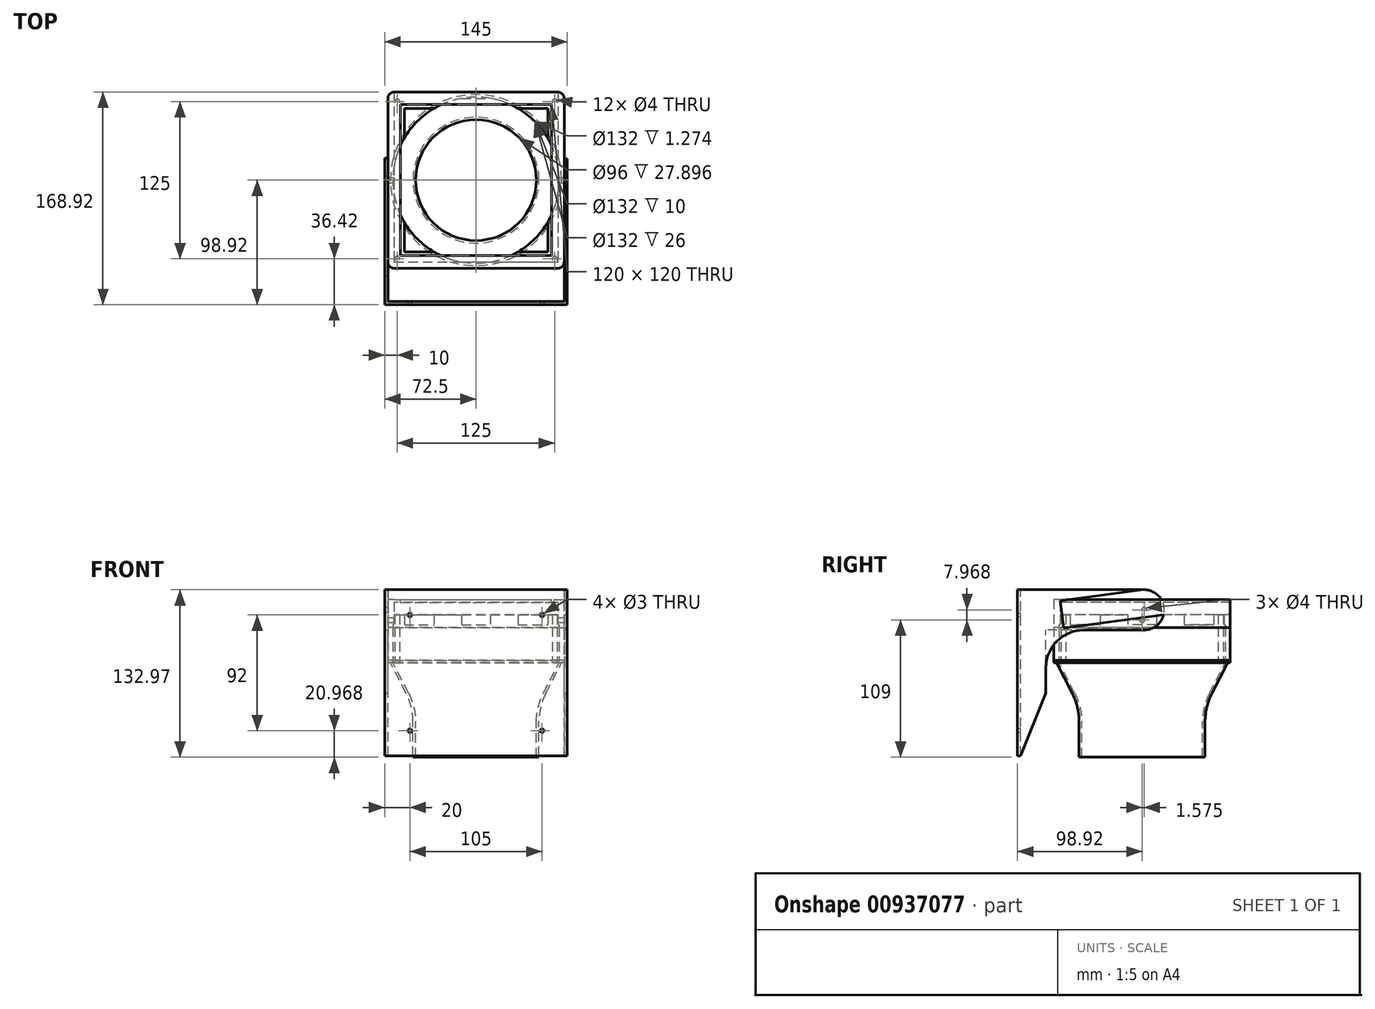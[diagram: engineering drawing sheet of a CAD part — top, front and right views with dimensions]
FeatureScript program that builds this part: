
annotation { "Feature Type Name" : "Feature", "Feature Type Description" : "" }
export const myFeature = defineFeature(function(context is Context, id is Id, definition is map)
    precondition{}
    {
        {
            var Q0;
            Q0=qCreatedBy(makeId("Top.planeOp"),FACE);
            var sketch = newSketch(context, id + "F0", { "sketchPlane" : qUnion([Q0])});
            skCircle(sketch, "E0", {"center": v(0, 0) * mm, "radius": 66 * mm});
            skLineSegment(sketch, "E1.bottom", {"start": v(-70, 70) * mm, "end": v(70, 70) * mm});
            skLineSegment(sketch, "E1.top", {"start": v(-70, -70) * mm, "end": v(70, -70) * mm});
            skLineSegment(sketch, "E1.left", {"start": v(-70, 70) * mm, "end": v(-70, -70) * mm});
            skLineSegment(sketch, "E1.right", {"start": v(70, 70) * mm, "end": v(70, -70) * mm});
            skLineSegment(sketch, "E2", {"start": v(-70, 0) * mm, "end": v(70, 0) * mm, "construction": true});
            skCircle(sketch, "E3", {"center": v(-62.5, 62.5) * mm, "radius": 2 * mm});
            skCircle(sketch, "E4", {"center": v(62.5, 62.5) * mm, "radius": 2 * mm});
            skCircle(sketch, "E5", {"center": v(62.5, -62.5) * mm, "radius": 2 * mm});
            skCircle(sketch, "E6", {"center": v(-62.5, -62.5) * mm, "radius": 2 * mm});
            skLineSegment(sketch, "E7", {"start": v(62.5, 62.5) * mm, "end": v(62.5, -62.5) * mm, "construction": true});
            skLineSegment(sketch, "E8", {"start": v(-62.5, 62.5) * mm, "end": v(62.5, 62.5) * mm, "construction": true});
            skLineSegment(sketch, "E9", {"start": v(-62.5, -62.5) * mm, "end": v(62.5, -62.5) * mm, "construction": true});
            skLineSegment(sketch, "E10", {"start": v(0, 62.5) * mm, "end": v(0, -62.5) * mm, "construction": true});
            skSolve(sketch);
        }
        {
            var Q0;
            Q0=makeQuery(id+"F0.imprint","IMPRINT",FACE,{"disambiguationData":[TD([[makeQuery(id+"F0.imprint","IMPRINT",EDGE,{"derivedFrom":sQuery(id+"F0.wireOp",EDGE,"E0")}),-1.0]])]});
            extrude(context, id + "F1", {"entities" : qUnion([Q0]), "depth" : 26 * mm, "offsetDistance" : 25 * mm});
        }
        {
            var Q0;
            Q0=makeQuery(id+"F1.opExtrude","SWEPT_EDGE",EDGE,{"disambiguationData":[OSD([sQuery(id+"F0.wireOp",EDGE,"E1.bottom"),sQuery(id+"F0.wireOp",EDGE,"E1.right")])]});
            var Q1;
            Q1=makeQuery(id+"F1.opExtrude","SWEPT_EDGE",EDGE,{"disambiguationData":[OSD([sQuery(id+"F0.wireOp",EDGE,"E1.top"),sQuery(id+"F0.wireOp",EDGE,"E1.right")])]});
            var Q2;
            Q2=makeQuery(id+"F1.opExtrude","SWEPT_EDGE",EDGE,{"disambiguationData":[OSD([sQuery(id+"F0.wireOp",EDGE,"E1.top"),sQuery(id+"F0.wireOp",EDGE,"E1.left")])]});
            var Q3;
            Q3=makeQuery(id+"F1.opExtrude","SWEPT_EDGE",EDGE,{"disambiguationData":[OSD([sQuery(id+"F0.wireOp",EDGE,"E1.bottom"),sQuery(id+"F0.wireOp",EDGE,"E1.left")])]});
            fillet(context, id + "F2", {"entities" : qUnion([Q0, Q1, Q2, Q3]), "radius" : 5 * mm, "tangentPropagation" : true, "allowEdgeOverflow" : false});
        }
        {
            var Q0;
            Q0=makeQuery(id+"F1.opExtrude","CAP_FACE",FACE,{"disambiguationData":[OSD([sQuery(id+"F0.wireOp",EDGE,"E0"),sQuery(id+"F0.wireOp",EDGE,"E1.bottom"),sQuery(id+"F0.wireOp",EDGE,"E1.top"),sQuery(id+"F0.wireOp",EDGE,"E1.left"),sQuery(id+"F0.wireOp",EDGE,"E1.right"),sQuery(id+"F0.wireOp",EDGE,"E3"),sQuery(id+"F0.wireOp",EDGE,"E4"),sQuery(id+"F0.wireOp",EDGE,"E5"),sQuery(id+"F0.wireOp",EDGE,"E6")])],"isStart":false});
            var sketch = newSketch(context, id + "F3", { "sketchPlane" : qUnion([Q0])});
            skCircle(sketch, "E11.0", {"center": v(0, 0) * mm, "radius": 66 * mm});
            skLineSegment(sketch, "E12.0.0", {"start": v(-70, 65) * mm, "end": v(-70, -65) * mm});
            skArc(sketch, "E12.0.1", {"start": v(-70, -65) * mm, "mid": v(-68.54, -68.54) * mm, "end": v(-65, -70) * mm});
            skLineSegment(sketch, "E12.0.2", {"start": v(-65, -70) * mm, "end": v(65, -70) * mm});
            skArc(sketch, "E12.0.3", {"start": v(65, -70) * mm, "mid": v(68.54, -68.54) * mm, "end": v(70, -65) * mm});
            skLineSegment(sketch, "E12.0.4", {"start": v(70, -65) * mm, "end": v(70, 65) * mm});
            skArc(sketch, "E12.0.5", {"start": v(70, 65) * mm, "mid": v(68.54, 68.54) * mm, "end": v(65, 70) * mm});
            skLineSegment(sketch, "E12.0.6", {"start": v(65, 70) * mm, "end": v(-65, 70) * mm});
            skArc(sketch, "E12.0.7", {"start": v(-65, 70) * mm, "mid": v(-68.54, 68.54) * mm, "end": v(-70, 65) * mm});
            skCircle(sketch, "E13.0", {"center": v(-62.5, -62.5) * mm, "radius": 2 * mm});
            skCircle(sketch, "E14.0", {"center": v(62.5, -62.5) * mm, "radius": 2 * mm});
            skCircle(sketch, "E15.0", {"center": v(62.5, 62.5) * mm, "radius": 2 * mm});
            skCircle(sketch, "E16.0", {"center": v(-62.5, 62.5) * mm, "radius": 2 * mm});
            skSolve(sketch);
        }
        {
            var Q0;
            Q0=makeQuery(id+"F3.imprint","IMPRINT",FACE,{"disambiguationData":[TD([[makeQuery(id+"F3.imprint","IMPRINT",EDGE,{"derivedFrom":sQuery(id+"F3.wireOp",EDGE,"E11.0")}),-1.0]])]});
            extrude(context, id + "F4", {"entities" : qUnion([Q0]), "depth" : 2 * mm, "offsetDistance" : 25 * mm});
        }
        {
            var Q0;
            Q0=makeQuery(id+"F4.opExtrude","CAP_FACE",FACE,{"disambiguationData":[OSD([sQuery(id+"F3.wireOp",EDGE,"E11.0"),sQuery(id+"F3.wireOp",EDGE,"E12.0.0"),sQuery(id+"F3.wireOp",EDGE,"E12.0.1"),sQuery(id+"F3.wireOp",EDGE,"E12.0.2"),sQuery(id+"F3.wireOp",EDGE,"E12.0.3"),sQuery(id+"F3.wireOp",EDGE,"E12.0.4"),sQuery(id+"F3.wireOp",EDGE,"E12.0.5"),sQuery(id+"F3.wireOp",EDGE,"E12.0.6"),sQuery(id+"F3.wireOp",EDGE,"E12.0.7"),sQuery(id+"F3.wireOp",EDGE,"E13.0"),sQuery(id+"F3.wireOp",EDGE,"E14.0"),sQuery(id+"F3.wireOp",EDGE,"E15.0"),sQuery(id+"F3.wireOp",EDGE,"E16.0")])],"isStart":false});
            var sketch = newSketch(context, id + "F5", { "sketchPlane" : qUnion([Q0])});
            skLineSegment(sketch, "E17.bottom", {"start": v(-65, 65) * mm, "end": v(65, 65) * mm});
            skLineSegment(sketch, "E17.top", {"start": v(-65, -65) * mm, "end": v(65, -65) * mm});
            skLineSegment(sketch, "E17.left", {"start": v(-65, 65) * mm, "end": v(-65, -65) * mm});
            skLineSegment(sketch, "E17.right", {"start": v(65, 65) * mm, "end": v(65, -65) * mm});
            skLineSegment(sketch, "E18", {"start": v(0, -65) * mm, "end": v(0, 65) * mm, "construction": true});
            skLineSegment(sketch, "E19.bottom", {"start": v(-57, 57) * mm, "end": v(57, 57) * mm});
            skLineSegment(sketch, "E19.top", {"start": v(-57, -57) * mm, "end": v(57, -57) * mm});
            skLineSegment(sketch, "E19.left", {"start": v(-57, 57) * mm, "end": v(-57, -57) * mm});
            skLineSegment(sketch, "E19.right", {"start": v(57, 57) * mm, "end": v(57, -57) * mm});
            skLineSegment(sketch, "E20", {"start": v(-57, 0) * mm, "end": v(57, 0) * mm, "construction": true});
            skSolve(sketch);
        }
        {
            var Q0;
            Q0=makeQuery(id+"F5.imprint","IMPRINT",FACE,{"disambiguationData":[TD([[makeQuery(id+"F5.imprint","IMPRINT",EDGE,{"derivedFrom":makeQuery(id+"F4.opExtrude","CAP_EDGE",EDGE,{"disambiguationData":[OSD([sQuery(id+"F3.wireOp",EDGE,"E12.0.0")])],"isStart":false})}),1.0]])]});
            var Q1;
            {var subQ0=sQuery(id+"F5.wireOp",EDGE,"E17.left");var subQ1=makeQuery(id+"F4.opExtrude","CAP_EDGE",EDGE,{"disambiguationData":[OSD([sQuery(id+"F3.wireOp",EDGE,"E11.0")])],"isStart":false});var subQ2=makeQuery(id+"F5.imprint","INTERSECT",VERTEX,{"disambiguationData":[OD(0.0)],"derivedFrom":[subQ1,subQ0]});Q1=makeQuery(id+"F5.imprint","IMPRINT",FACE,{"disambiguationData":[TD([[makeQuery(id+"F5.imprint","IMPRINT",EDGE,{"disambiguationData":[TD([[subQ2,-1.0]])],"derivedFrom":subQ0}),-1.0]])]});}
            var Q2;
            {var subQ0=sQuery(id+"F5.wireOp",EDGE,"E17.right");var subQ1=makeQuery(id+"F4.opExtrude","CAP_EDGE",EDGE,{"disambiguationData":[OSD([sQuery(id+"F3.wireOp",EDGE,"E11.0")])],"isStart":false});var subQ2=makeQuery(id+"F5.imprint","INTERSECT",VERTEX,{"disambiguationData":[OD(0.0)],"derivedFrom":[subQ1,subQ0]});Q2=makeQuery(id+"F5.imprint","IMPRINT",FACE,{"disambiguationData":[TD([[makeQuery(id+"F5.imprint","IMPRINT",EDGE,{"disambiguationData":[TD([[subQ2,-1.0]])],"derivedFrom":subQ0}),1.0]])]});}
            var Q3;
            {var subQ0=sQuery(id+"F5.wireOp",EDGE,"E17.bottom");var subQ1=makeQuery(id+"F4.opExtrude","CAP_EDGE",EDGE,{"disambiguationData":[OSD([sQuery(id+"F3.wireOp",EDGE,"E11.0")])],"isStart":false});var subQ2=makeQuery(id+"F5.imprint","INTERSECT",VERTEX,{"disambiguationData":[OD(0.0)],"derivedFrom":[subQ1,subQ0]});Q3=makeQuery(id+"F5.imprint","IMPRINT",FACE,{"disambiguationData":[TD([[makeQuery(id+"F5.imprint","IMPRINT",EDGE,{"disambiguationData":[TD([[subQ2,-1.0]])],"derivedFrom":subQ0}),1.0]])]});}
            var Q4;
            {var subQ0=sQuery(id+"F5.wireOp",EDGE,"E17.top");var subQ1=makeQuery(id+"F4.opExtrude","CAP_EDGE",EDGE,{"disambiguationData":[OSD([sQuery(id+"F3.wireOp",EDGE,"E11.0")])],"isStart":false});var subQ2=makeQuery(id+"F5.imprint","INTERSECT",VERTEX,{"disambiguationData":[OD(0.0)],"derivedFrom":[subQ1,subQ0]});Q4=makeQuery(id+"F5.imprint","IMPRINT",FACE,{"disambiguationData":[TD([[makeQuery(id+"F5.imprint","IMPRINT",EDGE,{"disambiguationData":[TD([[subQ2,-1.0]])],"derivedFrom":subQ0}),-1.0]])]});}
            extrude(context, id + "F6", {"entities" : qUnion([Q0, Q1, Q2, Q3, Q4]), "operationType" : NewBodyOperationType.ADD, "depth" : 20 * mm, "offsetDistance" : 25 * mm});
        }
        {
            var Q0;
            Q0=makeQuery(id+"F5.imprint","IMPRINT",FACE,{"disambiguationData":[TD([[makeQuery(id+"F5.imprint","IMPRINT",EDGE,{"derivedFrom":makeQuery(id+"F4.opExtrude","CAP_EDGE",EDGE,{"disambiguationData":[OSD([sQuery(id+"F3.wireOp",EDGE,"E13.0")])],"isStart":false})}),-1.0]])]});
            var Q1;
            Q1=makeQuery(id+"F5.imprint","IMPRINT",FACE,{"disambiguationData":[TD([[makeQuery(id+"F5.imprint","IMPRINT",EDGE,{"derivedFrom":makeQuery(id+"F4.opExtrude","CAP_EDGE",EDGE,{"disambiguationData":[OSD([sQuery(id+"F3.wireOp",EDGE,"E16.0")])],"isStart":false})}),-1.0]])]});
            var Q2;
            Q2=makeQuery(id+"F5.imprint","IMPRINT",FACE,{"disambiguationData":[TD([[makeQuery(id+"F5.imprint","IMPRINT",EDGE,{"derivedFrom":makeQuery(id+"F4.opExtrude","CAP_EDGE",EDGE,{"disambiguationData":[OSD([sQuery(id+"F3.wireOp",EDGE,"E15.0")])],"isStart":false})}),-1.0]])]});
            var Q3;
            Q3=makeQuery(id+"F5.imprint","IMPRINT",FACE,{"disambiguationData":[TD([[makeQuery(id+"F5.imprint","IMPRINT",EDGE,{"derivedFrom":makeQuery(id+"F4.opExtrude","CAP_EDGE",EDGE,{"disambiguationData":[OSD([sQuery(id+"F3.wireOp",EDGE,"E14.0")])],"isStart":false})}),-1.0]])]});
            extrude(context, id + "F7", {"entities" : qUnion([Q0, Q1, Q2, Q3]), "operationType" : NewBodyOperationType.ADD, "depth" : 8 * mm, "offsetDistance" : 25 * mm});
        }
        {
            var Q0;
            Q0=makeQuery(id+"F6.opExtrude","CAP_FACE",FACE,{"disambiguationData":[OSD([sQuery(id+"F3.wireOp",EDGE,"E12.0.0"),sQuery(id+"F3.wireOp",EDGE,"E12.0.1"),sQuery(id+"F3.wireOp",EDGE,"E12.0.2"),sQuery(id+"F3.wireOp",EDGE,"E12.0.3"),sQuery(id+"F3.wireOp",EDGE,"E12.0.4"),sQuery(id+"F3.wireOp",EDGE,"E12.0.5"),sQuery(id+"F3.wireOp",EDGE,"E12.0.6"),sQuery(id+"F3.wireOp",EDGE,"E12.0.7"),sQuery(id+"F5.wireOp",EDGE,"E17.bottom"),sQuery(id+"F5.wireOp",EDGE,"E17.top"),sQuery(id+"F5.wireOp",EDGE,"E17.left"),sQuery(id+"F5.wireOp",EDGE,"E17.right")])],"isStart":false});
            var sketch = newSketch(context, id + "F8", { "sketchPlane" : qUnion([Q0])});
            skLineSegment(sketch, "E21.0", {"start": v(-65, 65) * mm, "end": v(-65, -65) * mm});
            skLineSegment(sketch, "E22.0", {"start": v(-65, 65) * mm, "end": v(65, 65) * mm});
            skLineSegment(sketch, "E23.0", {"start": v(65, 65) * mm, "end": v(65, -65) * mm});
            skLineSegment(sketch, "E24.0", {"start": v(-65, -65) * mm, "end": v(65, -65) * mm});
            skLineSegment(sketch, "E25.0", {"start": v(-60, 60) * mm, "end": v(-60, -60) * mm});
            skLineSegment(sketch, "E25.1", {"start": v(-60, 60) * mm, "end": v(60, 60) * mm});
            skLineSegment(sketch, "E25.2", {"start": v(60, 60) * mm, "end": v(60, -60) * mm});
            skLineSegment(sketch, "E25.3", {"start": v(-60, -60) * mm, "end": v(60, -60) * mm});
            skSolve(sketch);
        }
        {
            var Q0;
            Q0=makeQuery(id+"F8.imprint","IMPRINT",FACE,{"disambiguationData":[TD([[makeQuery(id+"F8.imprint","IMPRINT",EDGE,{"derivedFrom":sQuery(id+"F8.wireOp",EDGE,"E21.0")}),1.0]])]});
            extrude(context, id + "F9", {"entities" : qUnion([Q0]), "operationType" : NewBodyOperationType.ADD, "oppositeDirection" : true, "depth" : 2 * mm, "offsetDistance" : 25 * mm});
        }
        {
            var Q0;
            Q0=makeQuery(id+"F6.opExtrude","SWEPT_FACE",FACE,{"disambiguationData":[OSD([sQuery(id+"F5.wireOp",EDGE,"E17.bottom")])]});
            var sketch = newSketch(context, id + "F10", { "sketchPlane" : qUnion([Q0])});
            skLineSegment(sketch, "E26", {"start": v(-11.45, 36) * mm, "end": v(11.45, 36) * mm});
            skSolve(sketch);
        }
        {
            var Q0;
            Q0=makeQuery(id+"F10.imprint","IMPRINT",FACE,{"disambiguationData":[TD([[makeQuery(id+"F10.imprint","IMPRINT",EDGE,{"derivedFrom":sQuery(id+"F10.wireOp",EDGE,"E26")}),1.0]])]});
            extrude(context, id + "F11", {"entities" : qUnion([Q0]), "operationType" : NewBodyOperationType.REMOVE, "oppositeDirection" : true, "depth" : 25 * mm, "offsetDistance" : 25 * mm});
        }
        {
            var Q0;
            Q0=makeQuery(id+"F1.opExtrude","CAP_FACE",FACE,{"disambiguationData":[OSD([sQuery(id+"F0.wireOp",EDGE,"E0"),sQuery(id+"F0.wireOp",EDGE,"E1.bottom"),sQuery(id+"F0.wireOp",EDGE,"E1.top"),sQuery(id+"F0.wireOp",EDGE,"E1.left"),sQuery(id+"F0.wireOp",EDGE,"E1.right"),sQuery(id+"F0.wireOp",EDGE,"E3"),sQuery(id+"F0.wireOp",EDGE,"E4"),sQuery(id+"F0.wireOp",EDGE,"E5"),sQuery(id+"F0.wireOp",EDGE,"E6")])],"isStart":true});
            var sketch = newSketch(context, id + "F12", { "sketchPlane" : qUnion([Q0])});
            skLineSegment(sketch, "E27.0.0", {"start": v(65, 70) * mm, "end": v(-65, 70) * mm});
            skArc(sketch, "E27.0.1", {"start": v(-65, 70) * mm, "mid": v(-68.54, 68.54) * mm, "end": v(-70, 65) * mm});
            skLineSegment(sketch, "E27.0.2", {"start": v(-70, 65) * mm, "end": v(-70, -65) * mm});
            skArc(sketch, "E27.0.3", {"start": v(-70, -65) * mm, "mid": v(-68.54, -68.54) * mm, "end": v(-65, -70) * mm});
            skLineSegment(sketch, "E27.0.4", {"start": v(-65, -70) * mm, "end": v(65, -70) * mm});
            skArc(sketch, "E27.0.5", {"start": v(65, -70) * mm, "mid": v(68.54, -68.54) * mm, "end": v(70, -65) * mm});
            skLineSegment(sketch, "E27.0.6", {"start": v(70, -65) * mm, "end": v(70, 65) * mm});
            skArc(sketch, "E27.0.7", {"start": v(70, 65) * mm, "mid": v(68.54, 68.54) * mm, "end": v(65, 70) * mm});
            skCircle(sketch, "E28.0", {"center": v(-62.5, -62.5) * mm, "radius": 2 * mm});
            skCircle(sketch, "E29.0", {"center": v(0, 0) * mm, "radius": 66 * mm});
            skCircle(sketch, "E30.0", {"center": v(-62.5, 62.5) * mm, "radius": 2 * mm});
            skCircle(sketch, "E31.0", {"center": v(62.5, 62.5) * mm, "radius": 2 * mm});
            skCircle(sketch, "E32.0", {"center": v(62.5, -62.5) * mm, "radius": 2 * mm});
            skSolve(sketch);
        }
        {
            var Q0;
            Q0=makeQuery(id+"F12.imprint","IMPRINT",FACE,{"disambiguationData":[TD([[makeQuery(id+"F12.imprint","IMPRINT",EDGE,{"derivedFrom":sQuery(id+"F12.wireOp",EDGE,"E27.0.0")}),-1.0]])]});
            extrude(context, id + "F13", {"entities" : qUnion([Q0]), "depth" : 2 * mm, "offsetDistance" : 25 * mm});
        }
        {
            var Q0;
            Q0=makeQuery(id+"F13.opExtrude","CAP_FACE",FACE,{"disambiguationData":[OSD([sQuery(id+"F12.wireOp",EDGE,"E27.0.0"),sQuery(id+"F12.wireOp",EDGE,"E27.0.1"),sQuery(id+"F12.wireOp",EDGE,"E27.0.2"),sQuery(id+"F12.wireOp",EDGE,"E27.0.3"),sQuery(id+"F12.wireOp",EDGE,"E27.0.4"),sQuery(id+"F12.wireOp",EDGE,"E27.0.5"),sQuery(id+"F12.wireOp",EDGE,"E27.0.6"),sQuery(id+"F12.wireOp",EDGE,"E27.0.7"),sQuery(id+"F12.wireOp",EDGE,"E28.0"),sQuery(id+"F12.wireOp",EDGE,"E29.0"),sQuery(id+"F12.wireOp",EDGE,"E30.0"),sQuery(id+"F12.wireOp",EDGE,"E31.0"),sQuery(id+"F12.wireOp",EDGE,"E32.0")])],"isStart":false});
            cPlane(context, id + "F14", {"entities" : qUnion([Q0]), "cplaneType" : CPlaneType.OFFSET, "offset" : 35 * mm, "width" : 150 * mm, "height" : 150 * mm});
        }
        {
            var Q0;
            Q0=qCreatedBy(id+"F14.planeOp",FACE);
            var sketch = newSketch(context, id + "F15", { "sketchPlane" : qUnion([Q0])});
            skCircle(sketch, "E33", {"center": v(0, 0) * mm, "radius": 48 * mm});
            skSolve(sketch);
        }
        {
            var Q0;
            Q0=qCreatedBy(makeId("Front.planeOp"),FACE);
            var sketch = newSketch(context, id + "F16", { "sketchPlane" : qUnion([Q0])});
            skLineSegment(sketch, "E34.0", {"start": v(48, -37) * mm, "end": v(-48, -37) * mm});
            skLineSegment(sketch, "E35.0", {"start": v(-66, -2) * mm, "end": v(66, -2) * mm});
            skLineSegment(sketch, "E36", {"start": v(-48, -37) * mm, "end": v(-66, -2) * mm});
            skLineSegment(sketch, "E37", {"start": v(-66, -2) * mm, "end": v(-68, -2) * mm});
            skLineSegment(sketch, "E38", {"start": v(-68, -2) * mm, "end": v(-50, -37) * mm});
            skLineSegment(sketch, "E39", {"start": v(-50, -37) * mm, "end": v(-48, -37) * mm});
            skSolve(sketch);
        }
        {
            var Q0;
            Q0=makeQuery(id+"F16.imprint","IMPRINT",FACE,{"disambiguationData":[TD([[makeQuery(id+"F16.imprint","IMPRINT",EDGE,{"derivedFrom":sQuery(id+"F16.wireOp",EDGE,"E36")}),1.0]])]});
            var Q1;
            Q1=sQuery(id+"F15.wireOp",EDGE,"E33");
            revolve(context, id + "F17", {"operationType" : NewBodyOperationType.ADD, "surfaceOperationType" : NewSurfaceOperationType.NEW, "entities" : qUnion([Q0]), "axis" : qUnion([Q1]), "revolveType" : RevolveType.FULL});
        }
        {
            var Q0;
            Q0=makeQuery(id+"F17.opRevolve","SWEPT_FACE",FACE,{"disambiguationData":[OSD([sQuery(id+"F16.wireOp",EDGE,"E39")])]});
            extrude(context, id + "F18", {"entities" : qUnion([Q0]), "operationType" : NewBodyOperationType.ADD, "depth" : 40 * mm, "offsetDistance" : 25 * mm});
        }
        {
            var Q0;
            {var subQ0=sQuery(id+"F3.wireOp",EDGE,"E12.0.4");Q0=makeQuery(id+"F6.boolean.opBoolean","MERGE",FACE,{"derivedFrom":[makeQuery(id+"F4.opExtrude","SWEPT_FACE",FACE,{"disambiguationData":[OSD([subQ0])]}),makeQuery(id+"F6.opExtrude","SWEPT_FACE",FACE,{"disambiguationData":[OSD([subQ0])]})]});}
            var sketch = newSketch(context, id + "F19", { "sketchPlane" : qUnion([Q0])});
            skLineSegment(sketch, "E40.0", {"start": v(11.45, 28) * mm, "end": v(-11.45, 28) * mm});
            skLineSegment(sketch, "E41.0", {"start": v(-11.45, 36) * mm, "end": v(-11.45, 28) * mm});
            skLineSegment(sketch, "E42.0", {"start": v(11.45, 36) * mm, "end": v(11.45, 28) * mm});
            skLineSegment(sketch, "E43", {"start": v(11.45, 32) * mm, "end": v(-11.45, 32) * mm, "construction": true});
            skCircle(sketch, "E44", {"center": v(0, 32) * mm, "radius": 2 * mm});
            skSolve(sketch);
        }
        {
            var Q0;
            Q0=makeQuery(id+"F19.imprint","IMPRINT",FACE,{"disambiguationData":[TD([[makeQuery(id+"F19.imprint","IMPRINT",EDGE,{"derivedFrom":sQuery(id+"F19.wireOp",EDGE,"E44")}),1.0]])]});
            extrude(context, id + "F20", {"entities" : qUnion([Q0]), "operationType" : NewBodyOperationType.REMOVE, "oppositeDirection" : true, "depth" : 200 * mm, "offsetDistance" : 25 * mm});
        }
        {
            var Q0;
            {var subQ0=sQuery(id+"F16.wireOp",EDGE,"E39");var subQ1=sQuery(id+"F16.wireOp",EDGE,"E38");Q0=makeQuery(id+"F18.boolean.opBoolean","MERGE",EDGE,{"derivedFrom":[makeQuery(id+"F17.opRevolve","SWEPT_EDGE",EDGE,{"disambiguationData":[OSD([subQ1,subQ0])]}),makeQuery(id+"F18.opExtrude","CAP_EDGE",EDGE,{"disambiguationData":[OSD([subQ1,subQ0])],"isStart":true})]});}
            var Q1;
            {var subQ0=sQuery(id+"F16.wireOp",EDGE,"E39");var subQ1=sQuery(id+"F16.wireOp",EDGE,"E36");Q1=makeQuery(id+"F18.boolean.opBoolean","MERGE",EDGE,{"derivedFrom":[makeQuery(id+"F17.opRevolve","SWEPT_EDGE",EDGE,{"disambiguationData":[OSD([subQ1,subQ0])]}),makeQuery(id+"F18.opExtrude","CAP_EDGE",EDGE,{"disambiguationData":[OSD([subQ1,subQ0])],"isStart":true})]});}
            fillet(context, id + "F21", {"entities" : qUnion([Q0, Q1]), "radius" : 50 * mm, "tangentPropagation" : true, "allowEdgeOverflow" : false});
        }
        {
            var Q0;
            Q0=makeQuery(id+"F17.opRevolve","SWEPT_EDGE",EDGE,{"disambiguationData":[OSD([sQuery(id+"F16.wireOp",EDGE,"E37"),sQuery(id+"F16.wireOp",EDGE,"E38")])]});
            var Q1;
            Q1=makeQuery(id+"F17.boolean.opBoolean","MERGE",EDGE,{"derivedFrom":[makeQuery(id+"F13.opExtrude","CAP_EDGE",EDGE,{"disambiguationData":[OSD([sQuery(id+"F12.wireOp",EDGE,"E29.0")])],"isStart":false}),makeQuery(id+"F17.opRevolve","SWEPT_EDGE",EDGE,{"disambiguationData":[OSD([sQuery(id+"F16.wireOp",EDGE,"E36"),sQuery(id+"F16.wireOp",EDGE,"E37")])]})]});
            fillet(context, id + "F22", {"entities" : qUnion([Q0, Q1]), "radius" : 3 * mm, "tangentPropagation" : true, "allowEdgeOverflow" : false});
        }
        {
            var Q0;
            {var subQ0=sQuery(id+"F3.wireOp",EDGE,"E12.0.0");Q0=makeQuery(id+"F6.boolean.opBoolean","MERGE",FACE,{"derivedFrom":[makeQuery(id+"F4.opExtrude","SWEPT_FACE",FACE,{"disambiguationData":[OSD([subQ0])]}),makeQuery(id+"F6.opExtrude","SWEPT_FACE",FACE,{"disambiguationData":[OSD([subQ0])]})]});}
            var sketch = newSketch(context, id + "F23", { "sketchPlane" : qUnion([Q0])});
            skCircle(sketch, "E45.0", {"center": v(0, 32) * mm, "radius": 2 * mm});
            skArc(sketch, "E46", {"start": v(-2.09, 47.86) * mm, "mid": v(-15.86, 29.91) * mm, "end": v(2.09, 16.14) * mm});
            skLineSegment(sketch, "E47", {"start": v(-2.09, 47.86) * mm, "end": v(97.06, 60.92) * mm});
            skLineSegment(sketch, "E48", {"start": v(2.09, 16.14) * mm, "end": v(101.23, 29.19) * mm});
            skLineSegment(sketch, "E49", {"start": v(97.06, 60.92) * mm, "end": v(101.23, 29.19) * mm});
            skLineSegment(sketch, "E50", {"start": v(99.25, 28.93) * mm, "end": v(95.07, 60.65) * mm});
            skSolve(sketch);
        }
        {
            var Q0;
            {var subQ3=sQuery(id+"F23.wireOp",EDGE,"E50");Q0=makeQuery(id+"F23.imprint","IMPRINT",FACE,{"disambiguationData":[TD([[makeQuery(id+"F23.imprint","IMPRINT",EDGE,{"derivedFrom":subQ3}),1.0]])]});}
            var Q1;
            Q1=makeQuery(id+"F23.imprint","IMPRINT",FACE,{"disambiguationData":[TD([[makeQuery(id+"F23.imprint","IMPRINT",EDGE,{"derivedFrom":sQuery(id+"F23.wireOp",EDGE,"E45.0")}),1.0]])]});
            var Q2;
            {var subQ0=sQuery(id+"F23.wireOp",EDGE,"E49");Q2=makeQuery(id+"F23.imprint","IMPRINT",FACE,{"disambiguationData":[TD([[makeQuery(id+"F23.imprint","IMPRINT",EDGE,{"derivedFrom":subQ0}),-1.0]])]});}
            extrude(context, id + "F24", {"entities" : qUnion([Q0, Q1, Q2]), "depth" : 2 * mm, "offsetDistance" : 25 * mm});
        }
        {
            var Q0;
            {var subQ0=sQuery(id+"F3.wireOp",EDGE,"E12.0.4");Q0=makeQuery(id+"F6.boolean.opBoolean","MERGE",FACE,{"derivedFrom":[makeQuery(id+"F4.opExtrude","SWEPT_FACE",FACE,{"disambiguationData":[OSD([subQ0])]}),makeQuery(id+"F6.opExtrude","SWEPT_FACE",FACE,{"disambiguationData":[OSD([subQ0])]})]});}
            var sketch = newSketch(context, id + "F25", { "sketchPlane" : qUnion([Q0])});
            skLineSegment(sketch, "E51.0.0", {"start": v(-97.06, 60.92) * mm, "end": v(2.09, 47.86) * mm});
            skArc(sketch, "E51.0.1", {"start": v(2.09, 47.86) * mm, "mid": v(15.86, 29.91) * mm, "end": v(-2.09, 16.14) * mm});
            skLineSegment(sketch, "E51.0.2", {"start": v(-2.09, 16.14) * mm, "end": v(-101.23, 29.19) * mm});
            skLineSegment(sketch, "E51.0.3", {"start": v(-101.23, 29.19) * mm, "end": v(-97.06, 60.92) * mm});
            skSolve(sketch);
        }
        {
            var Q0;
            {var subQ0=sQuery(id+"F25.wireOp",EDGE,"E51.0.2");Q0=makeQuery(id+"F25.imprint","IMPRINT",FACE,{"disambiguationData":[TD([[makeQuery(id+"F25.imprint","IMPRINT",EDGE,{"derivedFrom":subQ0}),-1.0]])]});}
            var Q1;
            Q1=makeQuery(id+"F25.imprint","IMPRINT",FACE,{"disambiguationData":[TD([[makeQuery(id+"F25.imprint","IMPRINT",EDGE,{"derivedFrom":makeQuery(id+"F20.boolean.opBoolean","COPY",EDGE,{"derivedFrom":makeQuery(id+"F20.opExtrude","CAP_EDGE",EDGE,{"disambiguationData":[OSD([sQuery(id+"F19.wireOp",EDGE,"E44")])],"isStart":true})})}),-1.0]])]});
            extrude(context, id + "F26", {"entities" : qUnion([Q0, Q1]), "depth" : 2 * mm, "offsetDistance" : 25 * mm});
        }
        {
            var Q0;
            {var subQ0=sQuery(id+"F23.wireOp",EDGE,"E49");Q0=makeQuery(id+"F23.imprint","IMPRINT",FACE,{"disambiguationData":[TD([[makeQuery(id+"F23.imprint","IMPRINT",EDGE,{"derivedFrom":subQ0}),-1.0]])]});}
            var Q1;
            Q1=makeQuery(id+"F26.opExtrude","CAP_FACE",FACE,{"disambiguationData":[OSD([sQuery(id+"F19.wireOp",EDGE,"E44"),sQuery(id+"F25.wireOp",EDGE,"E51.0.0"),sQuery(id+"F25.wireOp",EDGE,"E51.0.1"),sQuery(id+"F25.wireOp",EDGE,"E51.0.2"),sQuery(id+"F25.wireOp",EDGE,"E51.0.3")])],"isStart":true});
            extrude(context, id + "F27", {"entities" : qUnion([Q0]), "operationType" : NewBodyOperationType.ADD, "endBound" : BoundingType.UP_TO_SURFACE, "oppositeDirection" : true, "depth" : 25 * mm, "endBoundEntityFace" : qUnion([Q1]), "offsetDistance" : 25 * mm});
        }
        {
            var Q0;
            {var subQ0=sQuery(id+"F23.wireOp",EDGE,"E48");Q0=makeQuery(id+"F27.boolean.opBoolean","MERGE",FACE,{"derivedFrom":[makeQuery(id+"F24.opExtrude","SWEPT_FACE",FACE,{"disambiguationData":[OSD([subQ0])]}),makeQuery(id+"F26.opExtrude","SWEPT_FACE",FACE,{"disambiguationData":[OSD([sQuery(id+"F25.wireOp",EDGE,"E51.0.2")])]}),makeQuery(id+"F27.opExtrude","SWEPT_FACE",FACE,{"disambiguationData":[OSD([subQ0])]})]});}
            var sketch = newSketch(context, id + "F28", { "sketchPlane" : qUnion([Q0])});
            skLineSegment(sketch, "E52", {"start": v(72, 82.18) * mm, "end": v(70, 82.18) * mm});
            skLineSegment(sketch, "E53", {"start": v(-70, 82.18) * mm, "end": v(-72, 82.18) * mm});
            skSolve(sketch);
        }
        {
            var Q0;
            {var subQ6=sQuery(id+"F28.wireOp",EDGE,"E52");Q0=makeQuery(id+"F28.imprint","IMPRINT",FACE,{"disambiguationData":[TD([[makeQuery(id+"F28.imprint","IMPRINT",EDGE,{"derivedFrom":subQ6}),-1.0]])]});}
            extrude(context, id + "F29", {"entities" : qUnion([Q0]), "operationType" : NewBodyOperationType.ADD, "depth" : 100 * mm, "offsetDistance" : 25 * mm});
        }
        {
            var Q0;
            {var subQ2=sQuery(id+"F25.wireOp",EDGE,"E51.0.3");var subQ3=sQuery(id+"F25.wireOp",EDGE,"E51.0.2");var subQ4=makeQuery(id+"F26.opExtrude","CAP_EDGE",EDGE,{"disambiguationData":[OSD([subQ3])],"isStart":false});Q0=makeQuery(id+"F29.boolean.opBoolean","MERGE",FACE,{"derivedFrom":[makeQuery(id+"F26.opExtrude","CAP_FACE",FACE,{"disambiguationData":[OSD([sQuery(id+"F19.wireOp",EDGE,"E44"),sQuery(id+"F25.wireOp",EDGE,"E51.0.0"),sQuery(id+"F25.wireOp",EDGE,"E51.0.1"),subQ3,subQ2])],"isStart":false}),makeQuery(id+"F29.opExtrude","SWEPT_FACE",FACE,{"disambiguationData":[OSD([subQ3]),TDD([makeQuery(id+"F28.imprint","IMPRINT",EDGE,{"disambiguationData":[TD([[makeQuery(id+"F28.imprint","INTERSECT",VERTEX,{"derivedFrom":[subQ4,sQuery(id+"F28.wireOp",EDGE,"E52")]}),-1.0]])],"derivedFrom":subQ4})])]})]});}
            var sketch = newSketch(context, id + "F30", { "sketchPlane" : qUnion([Q0])});
            skLineSegment(sketch, "E54.0", {"start": v(-112.3, -70.22) * mm, "end": v(-95.07, 60.65) * mm});
            skLineSegment(sketch, "E55", {"start": v(-85.95, -23.25) * mm, "end": v(-112.3, -70.22) * mm});
            skSolve(sketch);
        }
        {
            var Q0;
            {var subQ0=sQuery(id+"F30.wireOp",EDGE,"E55");Q0=makeQuery(id+"F30.imprint","IMPRINT",FACE,{"disambiguationData":[TD([[makeQuery(id+"F30.imprint","IMPRINT",EDGE,{"derivedFrom":subQ0}),1.0]])]});}
            extrude(context, id + "F31", {"entities" : qUnion([Q0]), "operationType" : NewBodyOperationType.REMOVE, "oppositeDirection" : true, "depth" : 200 * mm, "offsetDistance" : 25 * mm});
        }
        {
            var Q0;
            Q0=makeQuery(id+"F29.opExtrude","CAP_EDGE",EDGE,{"disambiguationData":[OSD([sQuery(id+"F28.wireOp",EDGE,"E53")])],"isStart":true});
            var Q1;
            Q1=makeQuery(id+"F29.opExtrude","CAP_EDGE",EDGE,{"disambiguationData":[OSD([sQuery(id+"F28.wireOp",EDGE,"E52")])],"isStart":true});
            var Q2;
            {var subQ0=sQuery(id+"F28.wireOp",EDGE,"E52");var subQ1=sQuery(id+"F30.wireOp",EDGE,"E55");Q2=makeQuery(id+"F31.boolean.opBoolean","COPY",EDGE,{"disambiguationData":[topologyDisambiguationEdgeConnected([makeQuery(id+"F29.opExtrude","SWEPT_FACE",FACE,{"disambiguationData":[OSD([subQ0])]})])],"derivedFrom":makeQuery(id+"F31.opExtrude","SWEPT_EDGE",EDGE,{"disambiguationData":[OSD([sQuery(id+"F25.wireOp",EDGE,"E51.0.2"),subQ0,subQ1])]})});}
            var Q3;
            {var subQ0=sQuery(id+"F30.wireOp",EDGE,"E55");Q3=makeQuery(id+"F31.boolean.opBoolean","COPY",EDGE,{"disambiguationData":[topologyDisambiguationEdgeConnected([makeQuery(id+"F29.opExtrude","SWEPT_FACE",FACE,{"disambiguationData":[OSD([sQuery(id+"F28.wireOp",EDGE,"E53")])]})])],"derivedFrom":makeQuery(id+"F31.opExtrude","SWEPT_EDGE",EDGE,{"disambiguationData":[OSD([sQuery(id+"F25.wireOp",EDGE,"E51.0.2"),sQuery(id+"F28.wireOp",EDGE,"E52"),subQ0])]})});}
            fillet(context, id + "F32", {"entities" : qUnion([Q0, Q1, Q2, Q3]), "radius" : 30 * mm, "tangentPropagation" : true, "allowEdgeOverflow" : false});
        }
        {
            var Q0;
            {var subQ2=sQuery(id+"F25.wireOp",EDGE,"E51.0.3");var subQ3=sQuery(id+"F25.wireOp",EDGE,"E51.0.2");var subQ4=makeQuery(id+"F26.opExtrude","CAP_EDGE",EDGE,{"disambiguationData":[OSD([subQ3])],"isStart":false});Q0=makeQuery(id+"F29.boolean.opBoolean","MERGE",FACE,{"derivedFrom":[makeQuery(id+"F26.opExtrude","CAP_FACE",FACE,{"disambiguationData":[OSD([sQuery(id+"F19.wireOp",EDGE,"E44"),sQuery(id+"F25.wireOp",EDGE,"E51.0.0"),sQuery(id+"F25.wireOp",EDGE,"E51.0.1"),subQ3,subQ2])],"isStart":false}),makeQuery(id+"F29.opExtrude","SWEPT_FACE",FACE,{"disambiguationData":[OSD([subQ3]),TDD([makeQuery(id+"F28.imprint","IMPRINT",EDGE,{"disambiguationData":[TD([[makeQuery(id+"F28.imprint","INTERSECT",VERTEX,{"derivedFrom":[subQ4,sQuery(id+"F28.wireOp",EDGE,"E52")]}),-1.0]])],"derivedFrom":subQ4})])]})]});}
            extrude(context, id + "F33", {"entities" : qUnion([Q0]), "operationType" : NewBodyOperationType.ADD, "depth" : 0.5 * mm, "offsetDistance" : 25 * mm});
        }
        {
            var Q0;
            {var subQ0=sQuery(id+"F23.wireOp",EDGE,"E49");var subQ1=sQuery(id+"F23.wireOp",EDGE,"E48");var subQ2=makeQuery(id+"F24.opExtrude","CAP_EDGE",EDGE,{"disambiguationData":[OSD([subQ1])],"isStart":false});Q0=makeQuery(id+"F29.boolean.opBoolean","MERGE",FACE,{"derivedFrom":[makeQuery(id+"F24.opExtrude","CAP_FACE",FACE,{"disambiguationData":[OSD([sQuery(id+"F23.wireOp",EDGE,"E45.0"),sQuery(id+"F23.wireOp",EDGE,"E46"),sQuery(id+"F23.wireOp",EDGE,"E47"),subQ1,subQ0])],"isStart":false}),makeQuery(id+"F29.opExtrude","SWEPT_FACE",FACE,{"disambiguationData":[OSD([subQ1]),TDD([makeQuery(id+"F28.imprint","IMPRINT",EDGE,{"disambiguationData":[TD([[makeQuery(id+"F28.imprint","INTERSECT",VERTEX,{"derivedFrom":[subQ2,sQuery(id+"F28.wireOp",EDGE,"E53")]}),-1.0]])],"derivedFrom":subQ2})])]})]});}
            extrude(context, id + "F34", {"entities" : qUnion([Q0]), "operationType" : NewBodyOperationType.ADD, "depth" : 0.5 * mm, "offsetDistance" : 25 * mm});
        }
        {
            var Q0;
            {var subQ0=sQuery(id+"F25.wireOp",EDGE,"E51.0.3");var subQ1=sQuery(id+"F25.wireOp",EDGE,"E51.0.2");var subQ2=sQuery(id+"F23.wireOp",EDGE,"E49");var subQ3=sQuery(id+"F23.wireOp",EDGE,"E48");Q0=makeQuery(id+"F34.boolean.opBoolean","MERGE",FACE,{"derivedFrom":[makeQuery(id+"F33.boolean.opBoolean","MERGE",FACE,{"derivedFrom":[makeQuery(id+"F29.boolean.opBoolean","MERGE",FACE,{"derivedFrom":[makeQuery(id+"F27.boolean.opBoolean","MERGE",FACE,{"derivedFrom":[makeQuery(id+"F24.opExtrude","SWEPT_FACE",FACE,{"disambiguationData":[OSD([subQ2])]}),makeQuery(id+"F26.opExtrude","SWEPT_FACE",FACE,{"disambiguationData":[OSD([subQ0])]}),makeQuery(id+"F27.opExtrude","SWEPT_FACE",FACE,{"disambiguationData":[OSD([subQ2])]})]}),makeQuery(id+"F29.opExtrude","SWEPT_FACE",FACE,{"disambiguationData":[OSD([subQ3,subQ2,subQ1,subQ0])]})]}),makeQuery(id+"F33.opExtrude","SWEPT_FACE",FACE,{"disambiguationData":[OSD([subQ3,subQ2,subQ1,subQ0])]})]}),makeQuery(id+"F34.opExtrude","SWEPT_FACE",FACE,{"disambiguationData":[OSD([subQ3,subQ2,subQ1,subQ0])]})]});}
            extrude(context, id + "F35", {"entities" : qUnion([Q0]), "operationType" : NewBodyOperationType.ADD, "depth" : 0.5 * mm, "offsetDistance" : 25 * mm});
        }
        {
            var Q0;
            Q0=makeQuery(id+"F35.opExtrude","CAP_FACE",FACE,{"disambiguationData":[OSD([sQuery(id+"F23.wireOp",EDGE,"E48"),sQuery(id+"F23.wireOp",EDGE,"E49"),sQuery(id+"F25.wireOp",EDGE,"E51.0.2"),sQuery(id+"F25.wireOp",EDGE,"E51.0.3")])],"isStart":false});
            var sketch = newSketch(context, id + "F36", { "sketchPlane" : qUnion([Q0])});
            skCircle(sketch, "E56", {"center": v(-52.5, 27.73) * mm, "radius": 1.5 * mm});
            skCircle(sketch, "E57", {"center": v(52.5, 27.73) * mm, "radius": 1.5 * mm});
            skCircle(sketch, "E58", {"center": v(-52.5, -64.27) * mm, "radius": 1.5 * mm});
            skCircle(sketch, "E59", {"center": v(52.5, -64.27) * mm, "radius": 1.5 * mm});
            skSolve(sketch);
        }
        {
            var Q0;
            Q0=makeQuery(id+"F36.imprint","IMPRINT",FACE,{"disambiguationData":[TD([[makeQuery(id+"F36.imprint","IMPRINT",EDGE,{"derivedFrom":sQuery(id+"F36.wireOp",EDGE,"E56")}),1.0]])]});
            var Q1;
            Q1=makeQuery(id+"F36.imprint","IMPRINT",FACE,{"disambiguationData":[TD([[makeQuery(id+"F36.imprint","IMPRINT",EDGE,{"derivedFrom":sQuery(id+"F36.wireOp",EDGE,"E57")}),1.0]])]});
            var Q2;
            Q2=makeQuery(id+"F36.imprint","IMPRINT",FACE,{"disambiguationData":[TD([[makeQuery(id+"F36.imprint","IMPRINT",EDGE,{"derivedFrom":sQuery(id+"F36.wireOp",EDGE,"E59")}),1.0]])]});
            var Q3;
            Q3=makeQuery(id+"F36.imprint","IMPRINT",FACE,{"disambiguationData":[TD([[makeQuery(id+"F36.imprint","IMPRINT",EDGE,{"derivedFrom":sQuery(id+"F36.wireOp",EDGE,"E58")}),1.0]])]});
            extrude(context, id + "F37", {"entities" : qUnion([Q0, Q1, Q2, Q3]), "operationType" : NewBodyOperationType.REMOVE, "oppositeDirection" : true, "depth" : 25 * mm, "offsetDistance" : 25 * mm});
        }
        {
            var Q0;
            Q0=makeQuery(id+"F24.opExtrude","SWEPT_BODY",BODY,{"disambiguationData":[OSD([sQuery(id+"F23.wireOp",EDGE,"E45.0"),sQuery(id+"F23.wireOp",EDGE,"E46"),sQuery(id+"F23.wireOp",EDGE,"E47"),sQuery(id+"F23.wireOp",EDGE,"E48"),sQuery(id+"F23.wireOp",EDGE,"E49")])]});
            var Q1;
            Q1=makeQuery(id+"F9.opExtrude","CAP_EDGE",EDGE,{"disambiguationData":[OSD([sQuery(id+"F8.wireOp",EDGE,"E25.3")])],"isStart":true});
            transform(context, id + "F38", {"entities" : qUnion([Q0]), "transformType" : TransformType.ROTATION, "transformAxis" : qUnion([Q1]), "angle" : 7.5 * degree, "makeCopy" : false});
        }
    });
